# Revit family: Casement_28_I_Top_Hung_Standard
name_source: partatom
category: Generic Models
revit_build: Autodesk Revit 2014 (Build: 20130308_1515(x64)
units: mm (PartAtom-declared; Revit-internal decimal feet)

## types (20) — shared parameters
Aluminium Thickness = 1 mm  [stored 0.00328084 ft]
Bead SG Gap = 13 mm  [stored 0.0426509 ft]
Bottom Hung = No
Casement Dimension = 28 mm  [stored 0.0918635 ft]
Custom Sash Bottom Height = 554 mm  [stored 1.81759 ft]
Custom Sash Top Height = 554 mm  [stored 1.81759 ft]
Default Sill Height = 800 mm  [stored 2.62467 ft]
Depth Bead = 14 mm  [stored 0.0459318 ft]
Description = Window 28mm, Type I top hung
Frame Center Offset = 14 mm  [stored 0.0459318 ft]
Height Panel 1 = 540 mm  [stored 1.77165 ft]
Height Sash Top = 524 mm  [stored 1.71916 ft]
Height Sash Top Opening = 554 mm  [stored 1.81759 ft]
Limit Fixed Pane Height Max = 1800 mm
Limit Fixed Pane Height Min = 200 mm  [stored 0.656168 ft]
Limit Fixed Pane Width Max = 1500 mm
Limit Fixed Pane Width Min = 200 mm  [stored 0.656168 ft]
Limit Sash Bottom Height Min = 300 mm  [stored 0.984252 ft]
Limit Sash Top Height Max = 600 mm  [stored 1.9685 ft]
Limit Sash Top Height Min = 300 mm  [stored 0.984252 ft]
Limit Sash Width Max = 900 mm  [stored 2.95276 ft]
Limit Sash Width Min = 300 mm  [stored 0.984252 ft]
Limit Window Height Max = 1860 mm
Manufacturer = Crealco
Model = Casement 28
Offset Bead SG Center Reversed = 14 mm  [stored 0.0459318 ft]
Offset Sash 1 Top = 23 mm  [stored 0.0754593 ft]
Offset Sash 2 Top = 593 mm  [stored 1.94554 ft]
Offset Sash Left = 23 mm  [stored 0.0754593 ft]
Offset Transom 1 Top = 570 mm  [stored 1.87008 ft]
Offset Window Exterior = 14 mm  [stored 0.0459318 ft]
SG Gasket Thickness = 6 mm  [stored 0.019685 ft]
Sash Center Offset = 11 mm  [stored 0.0360892 ft]
Sash Overlap = 7 mm  [stored 0.0229659 ft]
Sash Spacing Inner = 8 mm  [stored 0.0262467 ft]
Single Glazing = Yes
Top Hung = Yes
URL = http://www.crealco.co.za
Wall Closure = By host
Width Bead = 15 mm  [stored 0.0492126 ft]
Width Profile = 30 mm  [stored 0.0984252 ft]
zero-valued in all types: Window Exterior Offset

## per-type parameters (varying)
- 28-1215DT-1000Pa: Area Pane Left Bottom=0.1 m²; Area Pane Left Middle=0.13 m²; Area Pane Left Top=0.23 m²; Area Pane Right=0.62 m²; Clearvue SHGC Value=0.89; Clearvue U Value=8.89; Custom Sash Width=554 mm  [stored 1.81759 ft]; Custom Windload=1000 mm; Custom Window Height=1190 mm; Custom Window Width=1190 mm; Depth Mullion=54 mm  [stored 0.177165 ft]; Energy Advantage SHGC Value=0.797; Energy Advantage U Value=6.79; Height=1190 mm; Height Panel 2=330 mm  [stored 1.08268 ft]; Height Panel 3=200 mm  [stored 0.656168 ft]; Height Panel 4=1130 mm; Height Sash Bottom=314 mm; Height Sash Bottom Opening=344 mm; Intruderprufe LowE SHGC Value=0.747; Intruderprufe LowE U Value=6.63; Intruderprufe SHGC Value=0.859; Intruderprufe U Value=8.83; Length Mullion=1190 mm; Length Transom=540 mm  [stored 1.77165 ft]; Limit Sash Bottom Height Max=344 mm; Limit Sash Bottom Height Max Based On Top Sash=344 mm; Limit Sash Bottom Height Max Calc=344 mm; Limit Window Height Min=1190 mm; Limit Window Width Max=2130 mm; Limit Window Width Min=830 mm  [stored 2.7231 ft]; Max Pane Area=0.62 m²; Mullion Depth Windload Based=54 mm  [stored 0.177165 ft]; Offset Mullion Left=570 mm  [stored 1.87008 ft]; Offset Panel 3 Bead Top=960 mm  [stored 3.14961 ft]; Offset Panel 4 Left=600 mm  [stored 1.9685 ft]; Offset Transom 2 Top=930 mm  [stored 3.05118 ft]; Width=1190 mm; Width Panel 1=540 mm  [stored 1.77165 ft]; Width Panel 2=540 mm  [stored 1.77165 ft]; Width Panel 3=540 mm  [stored 1.77165 ft]; Width Panel 4=560 mm  [stored 1.83727 ft]; Width Sash 1=524 mm  [stored 1.71916 ft]; Width Sash 2=524 mm  [stored 1.71916 ft]; Width Sash Opening=554 mm  [stored 1.81759 ft]; Windload Design=1000 mm
- 28-1215DT-2000Pa: Area Pane Left Bottom=0.15 m²; Area Pane Left Middle=0.23 m²; Area Pane Left Top=0.23 m²; Area Pane Right=0.78 m²; Clearvue SHGC Value=0.981; Clearvue U Value=8.96; Custom Sash Width=554 mm  [stored 1.81759 ft]; Custom Windload=2000 mm; Custom Window Height=1490 mm; Custom Window Width=1190 mm; Depth Mullion=70 mm  [stored 0.229659 ft]; Energy Advantage SHGC Value=0.798; Energy Advantage U Value=6.87; Height=1490 mm; Height Panel 2=540 mm  [stored 1.77165 ft]; Height Panel 3=290 mm  [stored 0.951444 ft]; Height Panel 4=1430 mm; Height Sash Bottom=524 mm  [stored 1.71916 ft]; Height Sash Bottom Opening=554 mm  [stored 1.81759 ft]; Intruderprufe LowE SHGC Value=0.748; Intruderprufe LowE U Value=6.71; Intruderprufe SHGC Value=0.845; Intruderprufe U Value=8.85; Length Mullion=1490 mm; Length Transom=540 mm  [stored 1.77165 ft]; Limit Sash Bottom Height Max=600 mm  [stored 1.9685 ft]; Limit Sash Bottom Height Max Based On Top Sash=644 mm  [stored 2.11286 ft]; Limit Sash Bottom Height Max Calc=600 mm  [stored 1.9685 ft]; Limit Window Height Min=1400 mm; Limit Window Width Max=2130 mm; Limit Window Width Min=830 mm  [stored 2.7231 ft]; Max Pane Area=0.78 m²; Mullion Depth Windload Based=70 mm  [stored 0.229659 ft]; Offset Mullion Left=570 mm  [stored 1.87008 ft]; Offset Panel 3 Bead Top=1170 mm; Offset Panel 4 Left=600 mm  [stored 1.9685 ft]; Offset Transom 2 Top=1140 mm; Width=1190 mm; Width Panel 1=540 mm  [stored 1.77165 ft]; Width Panel 2=540 mm  [stored 1.77165 ft]; Width Panel 3=540 mm  [stored 1.77165 ft]; Width Panel 4=560 mm  [stored 1.83727 ft]; Width Sash 1=524 mm  [stored 1.71916 ft]; Width Sash 2=524 mm  [stored 1.71916 ft]; Width Sash Opening=554 mm  [stored 1.81759 ft]; Windload Design=2000 mm
- 28-1515DT-1000Pa: Area Pane Left Bottom=0.15 m²; Area Pane Left Middle=0.23 m²; Area Pane Left Top=0.23 m²; Area Pane Right=1.21 m²; Clearvue SHGC Value=1.032; Clearvue U Value=9.65; Custom Sash Width=554 mm  [stored 1.81759 ft]; Custom Windload=1000 mm; Custom Window Height=1490 mm; Custom Window Width=1490 mm; Depth Mullion=54 mm  [stored 0.177165 ft]; Energy Advantage SHGC Value=0.919; Energy Advantage U Value=7.16; Height=1490 mm; Height Panel 2=540 mm  [stored 1.77165 ft]; Height Panel 3=290 mm  [stored 0.951444 ft]; Height Panel 4=1430 mm; Height Sash Bottom=524 mm  [stored 1.71916 ft]; Height Sash Bottom Opening=554 mm  [stored 1.81759 ft]; Intruderprufe LowE SHGC Value=0.864; Intruderprufe LowE U Value=7.01; Intruderprufe SHGC Value=0.99; Intruderprufe U Value=9.56; Length Mullion=1490 mm; Length Transom=540 mm  [stored 1.77165 ft]; Limit Sash Bottom Height Max=600 mm  [stored 1.9685 ft]; Limit Sash Bottom Height Max Based On Top Sash=644 mm  [stored 2.11286 ft]; Limit Sash Bottom Height Max Calc=600 mm  [stored 1.9685 ft]; Limit Window Height Min=1400 mm; Limit Window Width Max=2130 mm; Limit Window Width Min=830 mm  [stored 2.7231 ft]; Max Pane Area=1.21 m²; Mullion Depth Windload Based=54 mm  [stored 0.177165 ft]; Offset Mullion Left=570 mm  [stored 1.87008 ft]; Offset Panel 3 Bead Top=1170 mm; Offset Panel 4 Left=600 mm  [stored 1.9685 ft]; Offset Transom 2 Top=1140 mm; Width=1490 mm; Width Panel 1=540 mm  [stored 1.77165 ft]; Width Panel 2=540 mm  [stored 1.77165 ft]; Width Panel 3=540 mm  [stored 1.77165 ft]; Width Panel 4=860 mm  [stored 2.82152 ft]; Width Sash 1=524 mm  [stored 1.71916 ft]; Width Sash 2=524 mm  [stored 1.71916 ft]; Width Sash Opening=554 mm  [stored 1.81759 ft]; Windload Design=1000 mm
- 28-1515DT-1500Pa: Area Pane Left Bottom=0.15 m²; Area Pane Left Middle=0.23 m²; Area Pane Left Top=0.23 m²; Area Pane Right=1.21 m²; Clearvue SHGC Value=1.033; Clearvue U Value=9.71; Custom Sash Width=554 mm  [stored 1.81759 ft]; Custom Windload=1500 mm; Custom Window Height=1490 mm; Custom Window Width=1490 mm; Depth Mullion=70 mm  [stored 0.229659 ft]; Energy Advantage SHGC Value=0.921; Energy Advantage U Value=7.26; Height=1490 mm; Height Panel 2=540 mm  [stored 1.77165 ft]; Height Panel 3=290 mm  [stored 0.951444 ft]; Height Panel 4=1430 mm; Height Sash Bottom=524 mm  [stored 1.71916 ft]; Height Sash Bottom Opening=554 mm  [stored 1.81759 ft]; Intruderprufe LowE SHGC Value=0.864; Intruderprufe LowE U Value=7.08; Intruderprufe SHGC Value=0.978; Intruderprufe U Value=9.57; Length Mullion=1490 mm; Length Transom=540 mm  [stored 1.77165 ft]; Limit Sash Bottom Height Max=600 mm  [stored 1.9685 ft]; Limit Sash Bottom Height Max Based On Top Sash=644 mm  [stored 2.11286 ft]; Limit Sash Bottom Height Max Calc=600 mm  [stored 1.9685 ft]; Limit Window Height Min=1400 mm; Limit Window Width Max=2130 mm; Limit Window Width Min=830 mm  [stored 2.7231 ft]; Max Pane Area=1.21 m²; Mullion Depth Windload Based=70 mm  [stored 0.229659 ft]; Offset Mullion Left=570 mm  [stored 1.87008 ft]; Offset Panel 3 Bead Top=1170 mm; Offset Panel 4 Left=600 mm  [stored 1.9685 ft]; Offset Transom 2 Top=1140 mm; Width=1490 mm; Width Panel 1=540 mm  [stored 1.77165 ft]; Width Panel 2=540 mm  [stored 1.77165 ft]; Width Panel 3=540 mm  [stored 1.77165 ft]; Width Panel 4=860 mm  [stored 2.82152 ft]; Width Sash 1=524 mm  [stored 1.71916 ft]; Width Sash 2=524 mm  [stored 1.71916 ft]; Width Sash Opening=554 mm  [stored 1.81759 ft]; Windload Design=1500 mm
- 28-1815DT-1000Pa: Area Pane Left Bottom=0.23 m²; Area Pane Left Middle=0.38 m²; Area Pane Left Top=0.38 m²; Area Pane Right=1.21 m²; Clearvue SHGC Value=0.947; Clearvue U Value=8.79; Custom Sash Width=854 mm  [stored 2.80184 ft]; Custom Windload=1000 mm; Custom Window Height=1490 mm; Custom Window Width=1790 mm; Depth Mullion=54 mm  [stored 0.177165 ft]; Energy Advantage SHGC Value=0.848; Energy Advantage U Value=6.51; Height=1490 mm; Height Panel 2=540 mm  [stored 1.77165 ft]; Height Panel 3=290 mm  [stored 0.951444 ft]; Height Panel 4=1430 mm; Height Sash Bottom=524 mm  [stored 1.71916 ft]; Height Sash Bottom Opening=554 mm  [stored 1.81759 ft]; Intruderprufe LowE SHGC Value=0.793; Intruderprufe LowE U Value=6.36; Intruderprufe SHGC Value=0.915; Intruderprufe U Value=8.73; Length Mullion=1490 mm; Length Transom=840 mm  [stored 2.75591 ft]; Limit Sash Bottom Height Max=600 mm  [stored 1.9685 ft]; Limit Sash Bottom Height Max Based On Top Sash=644 mm  [stored 2.11286 ft]; Limit Sash Bottom Height Max Calc=600 mm  [stored 1.9685 ft]; Limit Window Height Min=1400 mm; Limit Window Width Max=2430 mm; Limit Window Width Min=1130 mm; Max Pane Area=1.21 m²; Mullion Depth Windload Based=54 mm  [stored 0.177165 ft]; Offset Mullion Left=870 mm  [stored 2.85433 ft]; Offset Panel 3 Bead Top=1170 mm; Offset Panel 4 Left=900 mm  [stored 2.95276 ft]; Offset Transom 2 Top=1140 mm; Width=1790 mm; Width Panel 1=840 mm  [stored 2.75591 ft]; Width Panel 2=840 mm  [stored 2.75591 ft]; Width Panel 3=840 mm  [stored 2.75591 ft]; Width Panel 4=860 mm  [stored 2.82152 ft]; Width Sash 1=824 mm; Width Sash 2=824 mm; Width Sash Opening=854 mm  [stored 2.80184 ft]; Windload Design=1000 mm
- 28-1815DT-1500Pa: Area Pane Left Bottom=0.23 m²; Area Pane Left Middle=0.38 m²; Area Pane Left Top=0.38 m²; Area Pane Right=1.21 m²; Clearvue SHGC Value=0.948; Clearvue U Value=8.83; Custom Sash Width=854 mm  [stored 2.80184 ft]; Custom Windload=1500 mm; Custom Window Height=1490 mm; Custom Window Width=1790 mm; Depth Mullion=70 mm  [stored 0.229659 ft]; Energy Advantage SHGC Value=0.849; Energy Advantage U Value=6.56; Height=1490 mm; Height Panel 2=540 mm  [stored 1.77165 ft]; Height Panel 3=290 mm  [stored 0.951444 ft]; Height Panel 4=1430 mm; Height Sash Bottom=524 mm  [stored 1.71916 ft]; Height Sash Bottom Opening=554 mm  [stored 1.81759 ft]; Intruderprufe LowE SHGC Value=0.794; Intruderprufe LowE U Value=6.42; Intruderprufe SHGC Value=0.906; Intruderprufe U Value=8.74; Length Mullion=1490 mm; Length Transom=840 mm  [stored 2.75591 ft]; Limit Sash Bottom Height Max=600 mm  [stored 1.9685 ft]; Limit Sash Bottom Height Max Based On Top Sash=644 mm  [stored 2.11286 ft]; Limit Sash Bottom Height Max Calc=600 mm  [stored 1.9685 ft]; Limit Window Height Min=1400 mm; Limit Window Width Max=2430 mm; Limit Window Width Min=1130 mm; Max Pane Area=1.21 m²; Mullion Depth Windload Based=70 mm  [stored 0.229659 ft]; Offset Mullion Left=870 mm  [stored 2.85433 ft]; Offset Panel 3 Bead Top=1170 mm; Offset Panel 4 Left=900 mm  [stored 2.95276 ft]; Offset Transom 2 Top=1140 mm; Width=1790 mm; Width Panel 1=840 mm  [stored 2.75591 ft]; Width Panel 2=840 mm  [stored 2.75591 ft]; Width Panel 3=840 mm  [stored 2.75591 ft]; Width Panel 4=860 mm  [stored 2.82152 ft]; Width Sash 1=824 mm; Width Sash 2=824 mm; Width Sash Opening=854 mm  [stored 2.80184 ft]; Windload Design=1500 mm
- 28-2415DT-1000Pa: Area Pane Left Bottom=0.23 m²; Area Pane Left Middle=0.38 m²; Area Pane Left Top=0.38 m²; Area Pane Right=2.06 m²; Clearvue SHGC Value=0; Clearvue U Value=7.9; Custom Sash Width=854 mm  [stored 2.80184 ft]; Custom Windload=1000 mm; Custom Window Height=1490 mm; Custom Window Width=2390 mm; Depth Mullion=54 mm  [stored 0.177165 ft]; Energy Advantage SHGC Value=0; Energy Advantage U Value=7.9; Height=1490 mm; Height Panel 2=540 mm  [stored 1.77165 ft]; Height Panel 3=290 mm  [stored 0.951444 ft]; Height Panel 4=1430 mm; Height Sash Bottom=524 mm  [stored 1.71916 ft]; Height Sash Bottom Opening=554 mm  [stored 1.81759 ft]; Intruderprufe LowE SHGC Value=0.935; Intruderprufe LowE U Value=6.88; Intruderprufe SHGC Value=1.073; Intruderprufe U Value=9.68; Length Mullion=1490 mm; Length Transom=840 mm  [stored 2.75591 ft]; Limit Sash Bottom Height Max=600 mm  [stored 1.9685 ft]; Limit Sash Bottom Height Max Based On Top Sash=644 mm  [stored 2.11286 ft]; Limit Sash Bottom Height Max Calc=600 mm  [stored 1.9685 ft]; Limit Window Height Min=1400 mm; Limit Window Width Max=2430 mm; Limit Window Width Min=1130 mm; Max Pane Area=2.06 m²; Mullion Depth Windload Based=54 mm  [stored 0.177165 ft]; Offset Mullion Left=870 mm  [stored 2.85433 ft]; Offset Panel 3 Bead Top=1170 mm; Offset Panel 4 Left=900 mm  [stored 2.95276 ft]; Offset Transom 2 Top=1140 mm; Width=2390 mm; Width Panel 1=840 mm  [stored 2.75591 ft]; Width Panel 2=840 mm  [stored 2.75591 ft]; Width Panel 3=840 mm  [stored 2.75591 ft]; Width Panel 4=1460 mm; Width Sash 1=824 mm; Width Sash 2=824 mm; Width Sash Opening=854 mm  [stored 2.80184 ft]; Windload Design=1000 mm
- 28-2415DT-1500Pa: Area Pane Left Bottom=0.23 m²; Area Pane Left Middle=0.38 m²; Area Pane Left Top=0.38 m²; Area Pane Right=2.06 m²; Clearvue SHGC Value=0; Clearvue U Value=7.9; Custom Sash Width=854 mm  [stored 2.80184 ft]; Custom Windload=1500 mm; Custom Window Height=1490 mm; Custom Window Width=2390 mm; Depth Mullion=70 mm  [stored 0.229659 ft]; Energy Advantage SHGC Value=0; Energy Advantage U Value=7.9; Height=1490 mm; Height Panel 2=540 mm  [stored 1.77165 ft]; Height Panel 3=290 mm  [stored 0.951444 ft]; Height Panel 4=1430 mm; Height Sash Bottom=524 mm  [stored 1.71916 ft]; Height Sash Bottom Opening=554 mm  [stored 1.81759 ft]; Intruderprufe LowE SHGC Value=0.936; Intruderprufe LowE U Value=6.93; Intruderprufe SHGC Value=1.065; Intruderprufe U Value=9.69; Length Mullion=1490 mm; Length Transom=840 mm  [stored 2.75591 ft]; Limit Sash Bottom Height Max=600 mm  [stored 1.9685 ft]; Limit Sash Bottom Height Max Based On Top Sash=644 mm  [stored 2.11286 ft]; Limit Sash Bottom Height Max Calc=600 mm  [stored 1.9685 ft]; Limit Window Height Min=1400 mm; Limit Window Width Max=2430 mm; Limit Window Width Min=1130 mm; Max Pane Area=2.06 m²; Mullion Depth Windload Based=70 mm  [stored 0.229659 ft]; Offset Mullion Left=870 mm  [stored 2.85433 ft]; Offset Panel 3 Bead Top=1170 mm; Offset Panel 4 Left=900 mm  [stored 2.95276 ft]; Offset Transom 2 Top=1140 mm; Width=2390 mm; Width Panel 1=840 mm  [stored 2.75591 ft]; Width Panel 2=840 mm  [stored 2.75591 ft]; Width Panel 3=840 mm  [stored 2.75591 ft]; Width Panel 4=1460 mm; Width Sash 1=824 mm; Width Sash 2=824 mm; Width Sash Opening=854 mm  [stored 2.80184 ft]; Windload Design=1500 mm
- 28-1218DT-1000Pa: Area Pane Left Bottom=0.31 m²; Area Pane Left Middle=0.23 m²; Area Pane Left Top=0.23 m²; Area Pane Right=0.95 m²; Clearvue SHGC Value=0.963; Clearvue U Value=9.37; Custom Sash Width=554 mm  [stored 1.81759 ft]; Custom Windload=1000 mm; Custom Window Height=1790 mm; Custom Window Width=1190 mm; Depth Mullion=70 mm  [stored 0.229659 ft]; Energy Advantage SHGC Value=0.863; Energy Advantage U Value=7.1; Height=1790 mm; Height Panel 2=540 mm  [stored 1.77165 ft]; Height Panel 3=590 mm; Height Panel 4=1730 mm; Height Sash Bottom=524 mm  [stored 1.71916 ft]; Height Sash Bottom Opening=554 mm  [stored 1.81759 ft]; Intruderprufe LowE SHGC Value=0.808; Intruderprufe LowE U Value=6.93; Intruderprufe SHGC Value=0.91; Intruderprufe U Value=9.24; Length Mullion=1790 mm; Length Transom=540 mm  [stored 1.77165 ft]; Limit Sash Bottom Height Max=600 mm  [stored 1.9685 ft]; Limit Sash Bottom Height Max Based On Top Sash=944 mm; Limit Sash Bottom Height Max Calc=600 mm  [stored 1.9685 ft]; Limit Window Height Min=1400 mm; Limit Window Width Max=2130 mm; Limit Window Width Min=830 mm  [stored 2.7231 ft]; Max Pane Area=0.95 m²; Mullion Depth Windload Based=70 mm  [stored 0.229659 ft]; Offset Mullion Left=570 mm  [stored 1.87008 ft]; Offset Panel 3 Bead Top=1170 mm; Offset Panel 4 Left=600 mm  [stored 1.9685 ft]; Offset Transom 2 Top=1140 mm; Width=1190 mm; Width Panel 1=540 mm  [stored 1.77165 ft]; Width Panel 2=540 mm  [stored 1.77165 ft]; Width Panel 3=540 mm  [stored 1.77165 ft]; Width Panel 4=560 mm  [stored 1.83727 ft]; Width Sash 1=524 mm  [stored 1.71916 ft]; Width Sash 2=524 mm  [stored 1.71916 ft]; Width Sash Opening=554 mm  [stored 1.81759 ft]; Windload Design=1000 mm
- 28-1518DT-1000Pa: Area Pane Left Bottom=0.31 m²; Area Pane Left Middle=0.23 m²; Area Pane Left Top=0.23 m²; Area Pane Right=1.46 m²; Clearvue SHGC Value=0; Clearvue U Value=7.9; Custom Sash Width=554 mm  [stored 1.81759 ft]; Custom Windload=1000 mm; Custom Window Height=1790 mm; Custom Window Width=1490 mm; Depth Mullion=70 mm  [stored 0.229659 ft]; Energy Advantage SHGC Value=0; Energy Advantage U Value=7.9; Height=1790 mm; Height Panel 2=540 mm  [stored 1.77165 ft]; Height Panel 3=590 mm; Height Panel 4=1730 mm; Height Sash Bottom=524 mm  [stored 1.71916 ft]; Height Sash Bottom Opening=554 mm  [stored 1.81759 ft]; Intruderprufe LowE SHGC Value=0.945; Intruderprufe LowE U Value=7.44; Intruderprufe SHGC Value=1.066; Intruderprufe U Value=10.17; Length Mullion=1790 mm; Length Transom=540 mm  [stored 1.77165 ft]; Limit Sash Bottom Height Max=600 mm  [stored 1.9685 ft]; Limit Sash Bottom Height Max Based On Top Sash=944 mm; Limit Sash Bottom Height Max Calc=600 mm  [stored 1.9685 ft]; Limit Window Height Min=1400 mm; Limit Window Width Max=2130 mm; Limit Window Width Min=830 mm  [stored 2.7231 ft]; Max Pane Area=1.46 m²; Mullion Depth Windload Based=70 mm  [stored 0.229659 ft]; Offset Mullion Left=570 mm  [stored 1.87008 ft]; Offset Panel 3 Bead Top=1170 mm; Offset Panel 4 Left=600 mm  [stored 1.9685 ft]; Offset Transom 2 Top=1140 mm; Width=1490 mm; Width Panel 1=540 mm  [stored 1.77165 ft]; Width Panel 2=540 mm  [stored 1.77165 ft]; Width Panel 3=540 mm  [stored 1.77165 ft]; Width Panel 4=860 mm  [stored 2.82152 ft]; Width Sash 1=524 mm  [stored 1.71916 ft]; Width Sash 2=524 mm  [stored 1.71916 ft]; Width Sash Opening=554 mm  [stored 1.81759 ft]; Windload Design=1000 mm
- 28-1818DT-1000Pa: Area Pane Left Bottom=0.48 m²; Area Pane Left Middle=0.38 m²; Area Pane Left Top=0.38 m²; Area Pane Right=1.46 m²; Clearvue SHGC Value=0; Clearvue U Value=7.9; Custom Sash Width=854 mm  [stored 2.80184 ft]; Custom Windload=1000 mm; Custom Window Height=1790 mm; Custom Window Width=1790 mm; Depth Mullion=70 mm  [stored 0.229659 ft]; Energy Advantage SHGC Value=0; Energy Advantage U Value=7.9; Height=1790 mm; Height Panel 2=540 mm  [stored 1.77165 ft]; Height Panel 3=590 mm; Height Panel 4=1730 mm; Height Sash Bottom=524 mm  [stored 1.71916 ft]; Height Sash Bottom Opening=554 mm  [stored 1.81759 ft]; Intruderprufe LowE SHGC Value=0.656; Intruderprufe LowE U Value=6.62; Intruderprufe SHGC Value=0.973; Intruderprufe U Value=9.13; Length Mullion=1790 mm; Length Transom=840 mm  [stored 2.75591 ft]; Limit Sash Bottom Height Max=600 mm  [stored 1.9685 ft]; Limit Sash Bottom Height Max Based On Top Sash=944 mm; Limit Sash Bottom Height Max Calc=600 mm  [stored 1.9685 ft]; Limit Window Height Min=1400 mm; Limit Window Width Max=2430 mm; Limit Window Width Min=1130 mm; Max Pane Area=1.46 m²; Mullion Depth Windload Based=70 mm  [stored 0.229659 ft]; Offset Mullion Left=870 mm  [stored 2.85433 ft]; Offset Panel 3 Bead Top=1170 mm; Offset Panel 4 Left=900 mm  [stored 2.95276 ft]; Offset Transom 2 Top=1140 mm; Width=1790 mm; Width Panel 1=840 mm  [stored 2.75591 ft]; Width Panel 2=840 mm  [stored 2.75591 ft]; Width Panel 3=840 mm  [stored 2.75591 ft]; Width Panel 4=860 mm  [stored 2.82152 ft]; Width Sash 1=824 mm; Width Sash 2=824 mm; Width Sash Opening=854 mm  [stored 2.80184 ft]; Windload Design=1000 mm
- 28-2418DT-1000Pa: Area Pane Left Bottom=0.48 m²; Area Pane Left Middle=0.38 m²; Area Pane Left Top=0.38 m²; Area Pane Right=2.49 m²; Clearvue SHGC Value=0; Clearvue U Value=7.9; Custom Sash Width=854 mm  [stored 2.80184 ft]; Custom Windload=1000 mm; Custom Window Height=1790 mm; Custom Window Width=2390 mm; Depth Mullion=70 mm  [stored 0.229659 ft]; Energy Advantage SHGC Value=0; Energy Advantage U Value=7.9; Height=1790 mm; Height Panel 2=540 mm  [stored 1.77165 ft]; Height Panel 3=590 mm; Height Panel 4=1730 mm; Height Sash Bottom=524 mm  [stored 1.71916 ft]; Height Sash Bottom Opening=554 mm  [stored 1.81759 ft]; Intruderprufe LowE SHGC Value=1.025; Intruderprufe LowE U Value=7.32; Intruderprufe SHGC Value=1.164; Intruderprufe U Value=10.33; Length Mullion=1790 mm; Length Transom=840 mm  [stored 2.75591 ft]; Limit Sash Bottom Height Max=600 mm  [stored 1.9685 ft]; Limit Sash Bottom Height Max Based On Top Sash=944 mm; Limit Sash Bottom Height Max Calc=600 mm  [stored 1.9685 ft]; Limit Window Height Min=1400 mm; Limit Window Width Max=2430 mm; Limit Window Width Min=1130 mm; Max Pane Area=2.49 m²; Mullion Depth Windload Based=70 mm  [stored 0.229659 ft]; Offset Mullion Left=870 mm  [stored 2.85433 ft]; Offset Panel 3 Bead Top=1170 mm; Offset Panel 4 Left=900 mm  [stored 2.95276 ft]; Offset Transom 2 Top=1140 mm; Width=2390 mm; Width Panel 1=840 mm  [stored 2.75591 ft]; Width Panel 2=840 mm  [stored 2.75591 ft]; Width Panel 3=840 mm  [stored 2.75591 ft]; Width Panel 4=1460 mm; Width Sash 1=824 mm; Width Sash 2=824 mm; Width Sash Opening=854 mm  [stored 2.80184 ft]; Windload Design=1000 mm
- 28-1215DT-1500Pa: Area Pane Left Bottom=0.1 m²; Area Pane Left Middle=0.13 m²; Area Pane Left Top=0.23 m²; Area Pane Right=0.62 m²; Clearvue SHGC Value=0.89; Clearvue U Value=8.89; Custom Sash Width=554 mm  [stored 1.81759 ft]; Custom Windload=1500 mm; Custom Window Height=1190 mm; Custom Window Width=1190 mm; Depth Mullion=54 mm  [stored 0.177165 ft]; Energy Advantage SHGC Value=0.797; Energy Advantage U Value=6.79; Height=1190 mm; Height Panel 2=330 mm  [stored 1.08268 ft]; Height Panel 3=200 mm  [stored 0.656168 ft]; Height Panel 4=1130 mm; Height Sash Bottom=314 mm; Height Sash Bottom Opening=344 mm; Intruderprufe LowE SHGC Value=0.747; Intruderprufe LowE U Value=6.63; Intruderprufe SHGC Value=0.859; Intruderprufe U Value=8.83; Length Mullion=1190 mm; Length Transom=540 mm  [stored 1.77165 ft]; Limit Sash Bottom Height Max=344 mm; Limit Sash Bottom Height Max Based On Top Sash=344 mm; Limit Sash Bottom Height Max Calc=344 mm; Limit Window Height Min=1190 mm; Limit Window Width Max=2130 mm; Limit Window Width Min=830 mm  [stored 2.7231 ft]; Max Pane Area=0.62 m²; Mullion Depth Windload Based=54 mm  [stored 0.177165 ft]; Offset Mullion Left=570 mm  [stored 1.87008 ft]; Offset Panel 3 Bead Top=960 mm  [stored 3.14961 ft]; Offset Panel 4 Left=600 mm  [stored 1.9685 ft]; Offset Transom 2 Top=930 mm  [stored 3.05118 ft]; Width=1190 mm; Width Panel 1=540 mm  [stored 1.77165 ft]; Width Panel 2=540 mm  [stored 1.77165 ft]; Width Panel 3=540 mm  [stored 1.77165 ft]; Width Panel 4=560 mm  [stored 1.83727 ft]; Width Sash 1=524 mm  [stored 1.71916 ft]; Width Sash 2=524 mm  [stored 1.71916 ft]; Width Sash Opening=554 mm  [stored 1.81759 ft]; Windload Design=1500 mm
- 28-1218DT-1500Pa: Area Pane Left Bottom=0.31 m²; Area Pane Left Middle=0.23 m²; Area Pane Left Top=0.23 m²; Area Pane Right=0.95 m²; Clearvue SHGC Value=0.963; Clearvue U Value=9.37; Custom Sash Width=554 mm  [stored 1.81759 ft]; Custom Windload=1500 mm; Custom Window Height=1790 mm; Custom Window Width=1190 mm; Depth Mullion=70 mm  [stored 0.229659 ft]; Energy Advantage SHGC Value=0.863; Energy Advantage U Value=7.1; Height=1790 mm; Height Panel 2=540 mm  [stored 1.77165 ft]; Height Panel 3=590 mm; Height Panel 4=1730 mm; Height Sash Bottom=524 mm  [stored 1.71916 ft]; Height Sash Bottom Opening=554 mm  [stored 1.81759 ft]; Intruderprufe LowE SHGC Value=0.808; Intruderprufe LowE U Value=6.93; Intruderprufe SHGC Value=0.91; Intruderprufe U Value=9.24; Length Mullion=1790 mm; Length Transom=540 mm  [stored 1.77165 ft]; Limit Sash Bottom Height Max=600 mm  [stored 1.9685 ft]; Limit Sash Bottom Height Max Based On Top Sash=944 mm; Limit Sash Bottom Height Max Calc=600 mm  [stored 1.9685 ft]; Limit Window Height Min=1400 mm; Limit Window Width Max=2130 mm; Limit Window Width Min=830 mm  [stored 2.7231 ft]; Max Pane Area=0.95 m²; Mullion Depth Windload Based=70 mm  [stored 0.229659 ft]; Offset Mullion Left=570 mm  [stored 1.87008 ft]; Offset Panel 3 Bead Top=1170 mm; Offset Panel 4 Left=600 mm  [stored 1.9685 ft]; Offset Transom 2 Top=1140 mm; Width=1190 mm; Width Panel 1=540 mm  [stored 1.77165 ft]; Width Panel 2=540 mm  [stored 1.77165 ft]; Width Panel 3=540 mm  [stored 1.77165 ft]; Width Panel 4=560 mm  [stored 1.83727 ft]; Width Sash 1=524 mm  [stored 1.71916 ft]; Width Sash 2=524 mm  [stored 1.71916 ft]; Width Sash Opening=554 mm  [stored 1.81759 ft]; Windload Design=1500 mm
- 28-1218DT-2000Pa: Area Pane Left Bottom=0.31 m²; Area Pane Left Middle=0.23 m²; Area Pane Left Top=0.23 m²; Area Pane Right=0.95 m²; Clearvue SHGC Value=0.963; Clearvue U Value=9.37; Custom Sash Width=554 mm  [stored 1.81759 ft]; Custom Windload=2000 mm; Custom Window Height=1790 mm; Custom Window Width=1190 mm; Depth Mullion=70 mm  [stored 0.229659 ft]; Energy Advantage SHGC Value=0.863; Energy Advantage U Value=7.1; Height=1790 mm; Height Panel 2=540 mm  [stored 1.77165 ft]; Height Panel 3=590 mm; Height Panel 4=1730 mm; Height Sash Bottom=524 mm  [stored 1.71916 ft]; Height Sash Bottom Opening=554 mm  [stored 1.81759 ft]; Intruderprufe LowE SHGC Value=0.808; Intruderprufe LowE U Value=6.93; Intruderprufe SHGC Value=0.91; Intruderprufe U Value=9.24; Length Mullion=1790 mm; Length Transom=540 mm  [stored 1.77165 ft]; Limit Sash Bottom Height Max=600 mm  [stored 1.9685 ft]; Limit Sash Bottom Height Max Based On Top Sash=944 mm; Limit Sash Bottom Height Max Calc=600 mm  [stored 1.9685 ft]; Limit Window Height Min=1400 mm; Limit Window Width Max=2130 mm; Limit Window Width Min=830 mm  [stored 2.7231 ft]; Max Pane Area=0.95 m²; Mullion Depth Windload Based=70 mm  [stored 0.229659 ft]; Offset Mullion Left=570 mm  [stored 1.87008 ft]; Offset Panel 3 Bead Top=1170 mm; Offset Panel 4 Left=600 mm  [stored 1.9685 ft]; Offset Transom 2 Top=1140 mm; Width=1190 mm; Width Panel 1=540 mm  [stored 1.77165 ft]; Width Panel 2=540 mm  [stored 1.77165 ft]; Width Panel 3=540 mm  [stored 1.77165 ft]; Width Panel 4=560 mm  [stored 1.83727 ft]; Width Sash 1=524 mm  [stored 1.71916 ft]; Width Sash 2=524 mm  [stored 1.71916 ft]; Width Sash Opening=554 mm  [stored 1.81759 ft]; Windload Design=2000 mm
- 28-1515DT-2000Pa: Area Pane Left Bottom=0.15 m²; Area Pane Left Middle=0.23 m²; Area Pane Left Top=0.23 m²; Area Pane Right=1.21 m²; Clearvue SHGC Value=1.033; Clearvue U Value=9.71; Custom Sash Width=554 mm  [stored 1.81759 ft]; Custom Windload=2000 mm; Custom Window Height=1490 mm; Custom Window Width=1490 mm; Depth Mullion=70 mm  [stored 0.229659 ft]; Energy Advantage SHGC Value=0.921; Energy Advantage U Value=7.26; Height=1490 mm; Height Panel 2=540 mm  [stored 1.77165 ft]; Height Panel 3=290 mm  [stored 0.951444 ft]; Height Panel 4=1430 mm; Height Sash Bottom=524 mm  [stored 1.71916 ft]; Height Sash Bottom Opening=554 mm  [stored 1.81759 ft]; Intruderprufe LowE SHGC Value=0.864; Intruderprufe LowE U Value=7.08; Intruderprufe SHGC Value=0.978; Intruderprufe U Value=9.57; Length Mullion=1490 mm; Length Transom=540 mm  [stored 1.77165 ft]; Limit Sash Bottom Height Max=600 mm  [stored 1.9685 ft]; Limit Sash Bottom Height Max Based On Top Sash=644 mm  [stored 2.11286 ft]; Limit Sash Bottom Height Max Calc=600 mm  [stored 1.9685 ft]; Limit Window Height Min=1400 mm; Limit Window Width Max=2130 mm; Limit Window Width Min=830 mm  [stored 2.7231 ft]; Max Pane Area=1.21 m²; Mullion Depth Windload Based=70 mm  [stored 0.229659 ft]; Offset Mullion Left=570 mm  [stored 1.87008 ft]; Offset Panel 3 Bead Top=1170 mm; Offset Panel 4 Left=600 mm  [stored 1.9685 ft]; Offset Transom 2 Top=1140 mm; Width=1490 mm; Width Panel 1=540 mm  [stored 1.77165 ft]; Width Panel 2=540 mm  [stored 1.77165 ft]; Width Panel 3=540 mm  [stored 1.77165 ft]; Width Panel 4=860 mm  [stored 2.82152 ft]; Width Sash 1=524 mm  [stored 1.71916 ft]; Width Sash 2=524 mm  [stored 1.71916 ft]; Width Sash Opening=554 mm  [stored 1.81759 ft]; Windload Design=2000 mm
- 28-1518DT-1500Pa: Area Pane Left Bottom=0.31 m²; Area Pane Left Middle=0.23 m²; Area Pane Left Top=0.23 m²; Area Pane Right=1.46 m²; Clearvue SHGC Value=0; Clearvue U Value=7.9; Custom Sash Width=554 mm  [stored 1.81759 ft]; Custom Windload=1500 mm; Custom Window Height=1790 mm; Custom Window Width=1490 mm; Depth Mullion=70 mm  [stored 0.229659 ft]; Energy Advantage SHGC Value=0; Energy Advantage U Value=7.9; Height=1790 mm; Height Panel 2=540 mm  [stored 1.77165 ft]; Height Panel 3=590 mm; Height Panel 4=1730 mm; Height Sash Bottom=524 mm  [stored 1.71916 ft]; Height Sash Bottom Opening=554 mm  [stored 1.81759 ft]; Intruderprufe LowE SHGC Value=0.945; Intruderprufe LowE U Value=7.44; Intruderprufe SHGC Value=1.066; Intruderprufe U Value=10.17; Length Mullion=1790 mm; Length Transom=540 mm  [stored 1.77165 ft]; Limit Sash Bottom Height Max=600 mm  [stored 1.9685 ft]; Limit Sash Bottom Height Max Based On Top Sash=944 mm; Limit Sash Bottom Height Max Calc=600 mm  [stored 1.9685 ft]; Limit Window Height Min=1400 mm; Limit Window Width Max=2130 mm; Limit Window Width Min=830 mm  [stored 2.7231 ft]; Max Pane Area=1.46 m²; Mullion Depth Windload Based=70 mm  [stored 0.229659 ft]; Offset Mullion Left=570 mm  [stored 1.87008 ft]; Offset Panel 3 Bead Top=1170 mm; Offset Panel 4 Left=600 mm  [stored 1.9685 ft]; Offset Transom 2 Top=1140 mm; Width=1490 mm; Width Panel 1=540 mm  [stored 1.77165 ft]; Width Panel 2=540 mm  [stored 1.77165 ft]; Width Panel 3=540 mm  [stored 1.77165 ft]; Width Panel 4=860 mm  [stored 2.82152 ft]; Width Sash 1=524 mm  [stored 1.71916 ft]; Width Sash 2=524 mm  [stored 1.71916 ft]; Width Sash Opening=554 mm  [stored 1.81759 ft]; Windload Design=1500 mm
- 28-1815DT-2000Pa: Area Pane Left Bottom=0.23 m²; Area Pane Left Middle=0.38 m²; Area Pane Left Top=0.38 m²; Area Pane Right=1.21 m²; Clearvue SHGC Value=0.948; Clearvue U Value=8.83; Custom Sash Width=854 mm  [stored 2.80184 ft]; Custom Windload=2000 mm; Custom Window Height=1490 mm; Custom Window Width=1790 mm; Depth Mullion=70 mm  [stored 0.229659 ft]; Energy Advantage SHGC Value=0.849; Energy Advantage U Value=6.56; Height=1490 mm; Height Panel 2=540 mm  [stored 1.77165 ft]; Height Panel 3=290 mm  [stored 0.951444 ft]; Height Panel 4=1430 mm; Height Sash Bottom=524 mm  [stored 1.71916 ft]; Height Sash Bottom Opening=554 mm  [stored 1.81759 ft]; Intruderprufe LowE SHGC Value=0.794; Intruderprufe LowE U Value=6.42; Intruderprufe SHGC Value=0.906; Intruderprufe U Value=8.74; Length Mullion=1490 mm; Length Transom=840 mm  [stored 2.75591 ft]; Limit Sash Bottom Height Max=600 mm  [stored 1.9685 ft]; Limit Sash Bottom Height Max Based On Top Sash=644 mm  [stored 2.11286 ft]; Limit Sash Bottom Height Max Calc=600 mm  [stored 1.9685 ft]; Limit Window Height Min=1400 mm; Limit Window Width Max=2430 mm; Limit Window Width Min=1130 mm; Max Pane Area=1.21 m²; Mullion Depth Windload Based=70 mm  [stored 0.229659 ft]; Offset Mullion Left=870 mm  [stored 2.85433 ft]; Offset Panel 3 Bead Top=1170 mm; Offset Panel 4 Left=900 mm  [stored 2.95276 ft]; Offset Transom 2 Top=1140 mm; Width=1790 mm; Width Panel 1=840 mm  [stored 2.75591 ft]; Width Panel 2=840 mm  [stored 2.75591 ft]; Width Panel 3=840 mm  [stored 2.75591 ft]; Width Panel 4=860 mm  [stored 2.82152 ft]; Width Sash 1=824 mm; Width Sash 2=824 mm; Width Sash Opening=854 mm  [stored 2.80184 ft]; Windload Design=2000 mm
- 28-1818DT-1500Pa: Area Pane Left Bottom=0.48 m²; Area Pane Left Middle=0.38 m²; Area Pane Left Top=0.38 m²; Area Pane Right=1.46 m²; Clearvue SHGC Value=0; Clearvue U Value=7.9; Custom Sash Width=854 mm  [stored 2.80184 ft]; Custom Windload=1500 mm; Custom Window Height=1790 mm; Custom Window Width=1790 mm; Depth Mullion=70 mm  [stored 0.229659 ft]; Energy Advantage SHGC Value=0; Energy Advantage U Value=7.9; Height=1790 mm; Height Panel 2=540 mm  [stored 1.77165 ft]; Height Panel 3=590 mm; Height Panel 4=1730 mm; Height Sash Bottom=524 mm  [stored 1.71916 ft]; Height Sash Bottom Opening=554 mm  [stored 1.81759 ft]; Intruderprufe LowE SHGC Value=0.656; Intruderprufe LowE U Value=6.62; Intruderprufe SHGC Value=0.973; Intruderprufe U Value=9.13; Length Mullion=1790 mm; Length Transom=840 mm  [stored 2.75591 ft]; Limit Sash Bottom Height Max=600 mm  [stored 1.9685 ft]; Limit Sash Bottom Height Max Based On Top Sash=944 mm; Limit Sash Bottom Height Max Calc=600 mm  [stored 1.9685 ft]; Limit Window Height Min=1400 mm; Limit Window Width Max=2430 mm; Limit Window Width Min=1130 mm; Max Pane Area=1.46 m²; Mullion Depth Windload Based=70 mm  [stored 0.229659 ft]; Offset Mullion Left=870 mm  [stored 2.85433 ft]; Offset Panel 3 Bead Top=1170 mm; Offset Panel 4 Left=900 mm  [stored 2.95276 ft]; Offset Transom 2 Top=1140 mm; Width=1790 mm; Width Panel 1=840 mm  [stored 2.75591 ft]; Width Panel 2=840 mm  [stored 2.75591 ft]; Width Panel 3=840 mm  [stored 2.75591 ft]; Width Panel 4=860 mm  [stored 2.82152 ft]; Width Sash 1=824 mm; Width Sash 2=824 mm; Width Sash Opening=854 mm  [stored 2.80184 ft]; Windload Design=1500 mm
- 28-2415DT-2000Pa: Area Pane Left Bottom=0.23 m²; Area Pane Left Middle=0.38 m²; Area Pane Left Top=0.38 m²; Area Pane Right=2.06 m²; Clearvue SHGC Value=0; Clearvue U Value=7.9; Custom Sash Width=854 mm  [stored 2.80184 ft]; Custom Windload=2000 mm; Custom Window Height=1490 mm; Custom Window Width=2390 mm; Depth Mullion=70 mm  [stored 0.229659 ft]; Energy Advantage SHGC Value=0; Energy Advantage U Value=7.9; Height=1490 mm; Height Panel 2=540 mm  [stored 1.77165 ft]; Height Panel 3=290 mm  [stored 0.951444 ft]; Height Panel 4=1430 mm; Height Sash Bottom=524 mm  [stored 1.71916 ft]; Height Sash Bottom Opening=554 mm  [stored 1.81759 ft]; Intruderprufe LowE SHGC Value=0.936; Intruderprufe LowE U Value=6.93; Intruderprufe SHGC Value=1.065; Intruderprufe U Value=9.69; Length Mullion=1490 mm; Length Transom=840 mm  [stored 2.75591 ft]; Limit Sash Bottom Height Max=600 mm  [stored 1.9685 ft]; Limit Sash Bottom Height Max Based On Top Sash=644 mm  [stored 2.11286 ft]; Limit Sash Bottom Height Max Calc=600 mm  [stored 1.9685 ft]; Limit Window Height Min=1400 mm; Limit Window Width Max=2430 mm; Limit Window Width Min=1130 mm; Max Pane Area=2.06 m²; Mullion Depth Windload Based=70 mm  [stored 0.229659 ft]; Offset Mullion Left=870 mm  [stored 2.85433 ft]; Offset Panel 3 Bead Top=1170 mm; Offset Panel 4 Left=900 mm  [stored 2.95276 ft]; Offset Transom 2 Top=1140 mm; Width=2390 mm; Width Panel 1=840 mm  [stored 2.75591 ft]; Width Panel 2=840 mm  [stored 2.75591 ft]; Width Panel 3=840 mm  [stored 2.75591 ft]; Width Panel 4=1460 mm; Width Sash 1=824 mm; Width Sash 2=824 mm; Width Sash Opening=854 mm  [stored 2.80184 ft]; Windload Design=2000 mm

note: [stored X ft] marks values corroborated as IEEE doubles in the binary element streams (Revit-internal decimal feet)

## geometry (parser evidence)
native form markers: Blend x4, Sweep x28
no freeform markers — native parametric forms only
